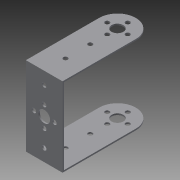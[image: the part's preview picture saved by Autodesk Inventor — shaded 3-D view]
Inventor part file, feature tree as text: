
AUTODESK INVENTOR PART (.ipt)
format: ipt  version: 2014 (Build 180170000, 170)  size: 158,720 bytes
history: native  units: mm
features: extrude x3, sketch x3, projected_geometry x1
ambient origin geometry x8: Origin, YZ Plane, XZ Plane, XY Plane, X Axis, Y Axis, Z Axis, Center Point
bodies: Solid1 (feature_tree)
feature tree (7):
  extrude  "Extrusion1"  Depth=25.0mm
  extrude  "Extrusion2"  Depth=3.0mm
  extrude  "Extrusion3"  Depth=1.0mm
  sketch  "Sketch1"  dims[d0=25.0mm d1=50.0mm]
  sketch  "Sketch2"  dims[d3=8.0mm d5=3.0mm]
  projected_geometry  "Projected Loop1"
  sketch  "Sketch3"  dims[d6=3.0mm d7=3.0mm d8=3.0mm d10=3.0mm d12=3.0mm d13=54.0mm d14=0.0mm d15=1.0mm d16=1.0mm d17=1.0mm d18=1.0mm d19=58.0mm d20=0.0mm d23=3.0mm d24=40.0mm d26=360.0deg d29=3.0mm d30=58.0mm d31=0.0mm]
